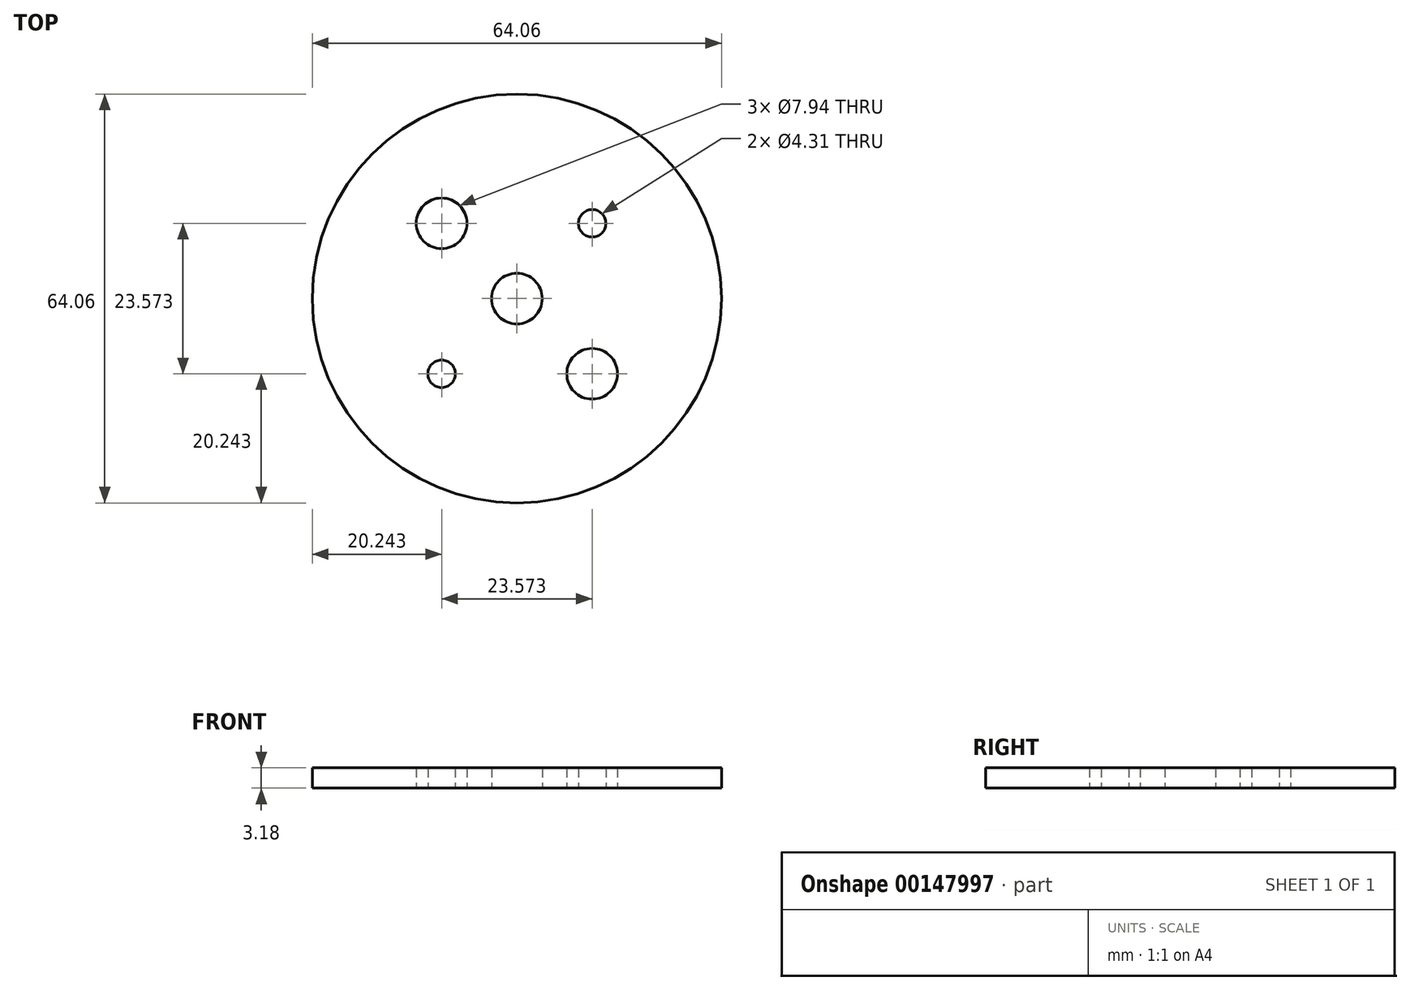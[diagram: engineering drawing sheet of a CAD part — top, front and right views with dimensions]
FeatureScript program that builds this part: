
annotation { "Feature Type Name" : "Feature", "Feature Type Description" : "" }
export const myFeature = defineFeature(function(context is Context, id is Id, definition is map)
    precondition{}
    {
        {
            var Q0;
            Q0=qCreatedBy(makeId("Top.planeOp"),FACE);
            var sketch = newSketch(context, id + "F0", { "sketchPlane" : qUnion([Q0])});
            skCircle(sketch, "E0", {"center": v(0, 0) * mm, "radius": 11.11 * mm, "construction": true});
            skLineSegment(sketch, "E1.bottom", {"start": v(11.79, -11.79) * mm, "end": v(-11.79, -11.79) * mm, "construction": true});
            skLineSegment(sketch, "E1.top", {"start": v(11.79, 11.79) * mm, "end": v(-11.79, 11.79) * mm, "construction": true});
            skLineSegment(sketch, "E1.left", {"start": v(11.79, -11.79) * mm, "end": v(11.79, 11.79) * mm, "construction": true});
            skLineSegment(sketch, "E1.right", {"start": v(-11.79, -11.79) * mm, "end": v(-11.79, 11.79) * mm, "construction": true});
            skCircle(sketch, "E2", {"center": v(-11.79, 11.79) * mm, "radius": 5.56 * mm, "construction": true});
            skCircle(sketch, "E3", {"center": v(-11.79, 11.79) * mm, "radius": 3.97 * mm});
            skCircle(sketch, "E4", {"center": v(11.79, 11.79) * mm, "radius": 2.15 * mm});
            skCircle(sketch, "E5", {"center": v(11.79, -11.79) * mm, "radius": 3.97 * mm});
            skCircle(sketch, "E6", {"center": v(-11.79, -11.79) * mm, "radius": 2.15 * mm});
            skCircle(sketch, "E7", {"center": v(0, 0) * mm, "radius": 32.03 * mm});
            skCircle(sketch, "E8", {"center": v(0, 0) * mm, "radius": 3.97 * mm});
            skSolve(sketch);
        }
        {
            var Q0;
            Q0=qSketchRegion(id+"F0",true);
            extrude(context, id + "F1", {"entities" : qUnion([Q0]), "depth" : 3.17 * mm});
        }
    });
